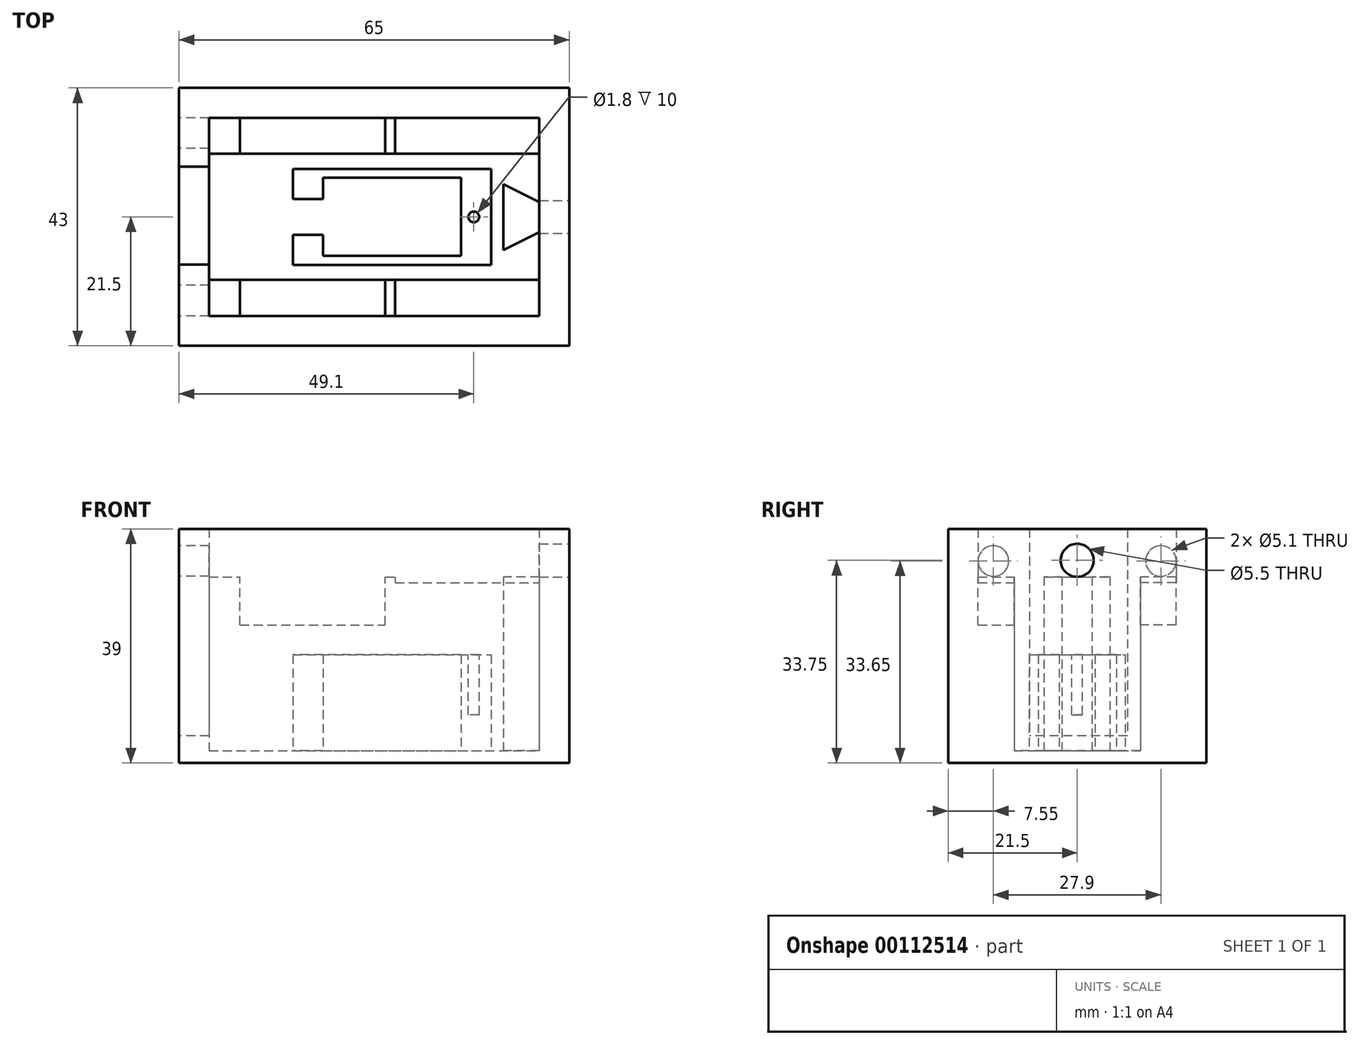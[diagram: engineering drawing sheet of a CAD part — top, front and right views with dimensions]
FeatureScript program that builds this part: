
annotation { "Feature Type Name" : "Feature", "Feature Type Description" : "" }
export const myFeature = defineFeature(function(context is Context, id is Id, definition is map)
    precondition{}
    {
        {
            var Q0;
            Q0=qCreatedBy(makeId("Top.planeOp"),FACE);
            var sketch = newSketch(context, id + "F0", { "sketchPlane" : qUnion([Q0])});
            skLineSegment(sketch, "E0.bottom", {"start": v(-32.5, 21.5) * mm, "end": v(32.5, 21.5) * mm});
            skLineSegment(sketch, "E0.top", {"start": v(-32.5, -21.5) * mm, "end": v(32.5, -21.5) * mm});
            skLineSegment(sketch, "E0.left", {"start": v(-32.5, 21.5) * mm, "end": v(-32.5, -21.5) * mm});
            skLineSegment(sketch, "E0.right", {"start": v(32.5, 21.5) * mm, "end": v(32.5, -21.5) * mm});
            skPoint(sketch, "E0.middle", {"position": v(0, 0) * mm});
            skSolve(sketch);
        }
        {
            var Q0;
            Q0 = qSketchRegion(id + "F0", true);
            extrude(context, id + "F1", {"entities" : qUnion([Q0]), "oppositeDirection" : true, "depth" : 2 * mm});
        }
        {
            var Q0;
            Q0=makeQuery(id+"F0.imprint","IMPRINT",FACE,{"disambiguationData":[TD([[makeQuery(id+"F0.imprint","IMPRINT",EDGE,{"derivedFrom":sQuery(id+"F0.wireOp",EDGE,"E0.bottom")}),-1.0]])]});
            var sketch = newSketch(context, id + "F2", { "sketchPlane" : qUnion([Q0])});
            skLineSegment(sketch, "E1", {"start": v(-32.5, 21.5) * mm, "end": v(-32.5, -21.5) * mm});
            skLineSegment(sketch, "E2", {"start": v(-32.5, -21.5) * mm, "end": v(32.5, -21.5) * mm});
            skLineSegment(sketch, "E3", {"start": v(32.5, -21.5) * mm, "end": v(32.5, 21.5) * mm});
            skLineSegment(sketch, "E4", {"start": v(32.5, 21.5) * mm, "end": v(-32.5, 21.5) * mm});
            skLineSegment(sketch, "E5", {"start": v(-27.5, 16.5) * mm, "end": v(-27.5, -16.5) * mm});
            skLineSegment(sketch, "E6", {"start": v(-27.5, -16.5) * mm, "end": v(27.5, -16.5) * mm});
            skLineSegment(sketch, "E7", {"start": v(27.5, -16.5) * mm, "end": v(27.5, 16.5) * mm});
            skLineSegment(sketch, "E8", {"start": v(27.5, 16.5) * mm, "end": v(-27.5, 16.5) * mm});
            skSolve(sketch);
        }
        {
            var Q0;
            Q0=makeQuery(id+"F2.imprint","IMPRINT",FACE,{"disambiguationData":[TD([[makeQuery(id+"F2.imprint","IMPRINT",EDGE,{"derivedFrom":sQuery(id+"F2.wireOp",EDGE,"E1")}),1.0]])]});
            extrude(context, id + "F3", {"entities" : qUnion([Q0]), "operationType" : NewBodyOperationType.ADD, "depth" : 37 * mm});
        }
        {
            var Q0;
            Q0=makeQuery(id+"F1.opExtrude","CAP_FACE",FACE,{"disambiguationData":[OSD([sQuery(id+"F0.wireOp",EDGE,"E0.bottom"),sQuery(id+"F0.wireOp",EDGE,"E0.top"),sQuery(id+"F0.wireOp",EDGE,"E0.left"),sQuery(id+"F0.wireOp",EDGE,"E0.right")])],"isStart":true});
            var sketch = newSketch(context, id + "F4", { "sketchPlane" : qUnion([Q0])});
            skLineSegment(sketch, "E9.bottom", {"start": v(-13.5, -8) * mm, "end": v(19.5, -8) * mm});
            skLineSegment(sketch, "E9.top", {"start": v(-13.5, 8) * mm, "end": v(19.5, 8) * mm});
            skLineSegment(sketch, "E9.left", {"start": v(-13.5, -8) * mm, "end": v(-13.5, 8) * mm});
            skLineSegment(sketch, "E9.right", {"start": v(19.5, -8) * mm, "end": v(19.5, 8) * mm});
            skPoint(sketch, "E9.middle", {"position": v(3, 0) * mm});
            skLineSegment(sketch, "E10", {"start": v(14.5, -6.5) * mm, "end": v(14.5, 6.5) * mm});
            skLineSegment(sketch, "E11", {"start": v(14.5, 6.5) * mm, "end": v(-8.5, 6.5) * mm});
            skLineSegment(sketch, "E12", {"start": v(-8.5, 6.5) * mm, "end": v(-8.5, -6.5) * mm});
            skLineSegment(sketch, "E13", {"start": v(-8.5, -6.5) * mm, "end": v(14.5, -6.5) * mm});
            skSolve(sketch);
        }
        {
            var Q0;
            Q0=makeQuery(id+"F4.imprint","IMPRINT",FACE,{"disambiguationData":[TD([[makeQuery(id+"F4.imprint","IMPRINT",EDGE,{"derivedFrom":sQuery(id+"F4.wireOp",EDGE,"E9.bottom")}),1.0]])]});
            extrude(context, id + "F5", {"entities" : qUnion([Q0]), "operationType" : NewBodyOperationType.ADD, "depth" : 16 * mm});
        }
        {
            var Q0;
            Q0=makeQuery(id+"F5.opExtrude","CAP_FACE",FACE,{"disambiguationData":[OSD([sQuery(id+"F4.wireOp",EDGE,"E9.bottom"),sQuery(id+"F4.wireOp",EDGE,"E9.top"),sQuery(id+"F4.wireOp",EDGE,"E9.left"),sQuery(id+"F4.wireOp",EDGE,"E9.right"),sQuery(id+"F4.wireOp",EDGE,"E10"),sQuery(id+"F4.wireOp",EDGE,"E11"),sQuery(id+"F4.wireOp",EDGE,"E12"),sQuery(id+"F4.wireOp",EDGE,"E13")])],"isStart":false});
            var sketch = newSketch(context, id + "F6", { "sketchPlane" : qUnion([Q0])});
            skCircle(sketch, "E14", {"center": v(16.6, 0) * mm, "radius": 0.9 * mm});
            skCircle(sketch, "E15", {"center": v(-10.6, 0) * mm, "radius": 0.9 * mm});
            skSolve(sketch);
        }
        {
            var Q0;
            Q0=makeQuery(id+"F6.imprint","IMPRINT",FACE,{"disambiguationData":[TD([[makeQuery(id+"F6.imprint","IMPRINT",EDGE,{"derivedFrom":sQuery(id+"F6.wireOp",EDGE,"E14")}),1.0]])]});
            var Q1;
            Q1=makeQuery(id+"F6.imprint","IMPRINT",FACE,{"disambiguationData":[TD([[makeQuery(id+"F6.imprint","IMPRINT",EDGE,{"derivedFrom":sQuery(id+"F6.wireOp",EDGE,"E15")}),1.0]])]});
            var Q2;
            Q2=sQuery(id+"F6.wireOp",EDGE,"E14");
            extrude(context, id + "F7", {"entities" : qUnion([Q0, Q1]), "operationType" : NewBodyOperationType.REMOVE, "surfaceEntities" : qUnion([Q2]), "oppositeDirection" : true, "depth" : 10 * mm});
        }
        {
            var Q0;
            Q0=makeQuery(id+"F5.boolean.opBoolean","SPLIT",FACE,{"disambiguationData":[TD([makeQuery(id+"F3.opExtrude","SWEPT_FACE",FACE,{"disambiguationData":[OSD([sQuery(id+"F2.wireOp",EDGE,"E5")])]})])],"derivedFrom":makeQuery(id+"F1.opExtrude","CAP_FACE",FACE,{"disambiguationData":[OSD([sQuery(id+"F0.wireOp",EDGE,"E0.bottom"),sQuery(id+"F0.wireOp",EDGE,"E0.top"),sQuery(id+"F0.wireOp",EDGE,"E0.left"),sQuery(id+"F0.wireOp",EDGE,"E0.right")])],"isStart":true})});
            var sketch = newSketch(context, id + "F8", { "sketchPlane" : qUnion([Q0])});
            skLineSegment(sketch, "E16.bottom", {"start": v(-27.5, -16.5) * mm, "end": v(27.5, -16.5) * mm});
            skLineSegment(sketch, "E16.top", {"start": v(-27.5, -10.5) * mm, "end": v(27.5, -10.5) * mm});
            skLineSegment(sketch, "E16.left", {"start": v(-27.5, -16.5) * mm, "end": v(-27.5, -10.5) * mm});
            skLineSegment(sketch, "E16.right", {"start": v(27.5, -16.5) * mm, "end": v(27.5, -10.5) * mm});
            skLineSegment(sketch, "E17.bottom", {"start": v(27.5, 16.5) * mm, "end": v(-27.5, 16.5) * mm});
            skLineSegment(sketch, "E17.top", {"start": v(27.5, 10.5) * mm, "end": v(-27.5, 10.5) * mm});
            skLineSegment(sketch, "E17.left", {"start": v(27.5, 16.5) * mm, "end": v(27.5, 10.5) * mm});
            skLineSegment(sketch, "E17.right", {"start": v(-27.5, 16.5) * mm, "end": v(-27.5, 10.5) * mm});
            skSolve(sketch);
        }
        {
            var Q0;
            Q0 = qSketchRegion(id + "F8", true);
            extrude(context, id + "F9", {"entities" : qUnion([Q0]), "operationType" : NewBodyOperationType.ADD, "depth" : 28 * mm});
        }
        {
            var Q0;
            Q0=makeQuery(id+"F3.boolean.opBoolean","MERGE",FACE,{"derivedFrom":[makeQuery(id+"F1.opExtrude","SWEPT_FACE",FACE,{"disambiguationData":[OSD([sQuery(id+"F0.wireOp",EDGE,"E0.left")])]}),makeQuery(id+"F3.opExtrude","SWEPT_FACE",FACE,{"disambiguationData":[OSD([sQuery(id+"F2.wireOp",EDGE,"E1")])]})]});
            var sketch = newSketch(context, id + "F10", { "sketchPlane" : qUnion([Q0])});
            skCircle(sketch, "E18", {"center": v(13.95, 31.65) * mm, "radius": 2.55 * mm});
            skCircle(sketch, "E19", {"center": v(-13.95, 31.65) * mm, "radius": 2.55 * mm});
            skSolve(sketch);
        }
        {
            var Q0;
            Q0=makeQuery(id+"F10.imprint","IMPRINT",FACE,{"disambiguationData":[TD([[makeQuery(id+"F10.imprint","IMPRINT",EDGE,{"derivedFrom":sQuery(id+"F10.wireOp",EDGE,"E18")}),1.0]])]});
            var Q1;
            Q1=makeQuery(id+"F10.imprint","IMPRINT",FACE,{"disambiguationData":[TD([[makeQuery(id+"F10.imprint","IMPRINT",EDGE,{"derivedFrom":sQuery(id+"F10.wireOp",EDGE,"E19")}),1.0]])]});
            extrude(context, id + "F11", {"entities" : qUnion([Q0, Q1]), "operationType" : NewBodyOperationType.REMOVE, "oppositeDirection" : true, "depth" : 25 * mm});
        }
        {
            var Q0;
            Q0=makeQuery(id+"F3.boolean.opBoolean","MERGE",FACE,{"derivedFrom":[makeQuery(id+"F1.opExtrude","SWEPT_FACE",FACE,{"disambiguationData":[OSD([sQuery(id+"F0.wireOp",EDGE,"E0.right")])]}),makeQuery(id+"F3.opExtrude","SWEPT_FACE",FACE,{"disambiguationData":[OSD([sQuery(id+"F2.wireOp",EDGE,"E3")])]})]});
            var sketch = newSketch(context, id + "F12", { "sketchPlane" : qUnion([Q0])});
            skCircle(sketch, "E20", {"center": v(0, 31.75) * mm, "radius": 2.75 * mm});
            skSolve(sketch);
        }
        {
            var Q0;
            Q0=makeQuery(id+"F12.imprint","IMPRINT",FACE,{"disambiguationData":[TD([[makeQuery(id+"F12.imprint","IMPRINT",EDGE,{"derivedFrom":sQuery(id+"F12.wireOp",EDGE,"E20")}),1.0]])]});
            extrude(context, id + "F13", {"entities" : qUnion([Q0]), "operationType" : NewBodyOperationType.REMOVE, "oppositeDirection" : true, "depth" : 25 * mm});
        }
        {
            var Q0;
            Q0=makeQuery(id+"F5.boolean.opBoolean","SPLIT",FACE,{"disambiguationData":[TD([makeQuery(id+"F3.opExtrude","SWEPT_FACE",FACE,{"disambiguationData":[OSD([sQuery(id+"F2.wireOp",EDGE,"E5")])]})])],"derivedFrom":makeQuery(id+"F1.opExtrude","CAP_FACE",FACE,{"disambiguationData":[OSD([sQuery(id+"F0.wireOp",EDGE,"E0.bottom"),sQuery(id+"F0.wireOp",EDGE,"E0.top"),sQuery(id+"F0.wireOp",EDGE,"E0.left"),sQuery(id+"F0.wireOp",EDGE,"E0.right")])],"isStart":true})});
            var sketch = newSketch(context, id + "F14", { "sketchPlane" : qUnion([Q0])});
            skLineSegment(sketch, "E21", {"start": v(27.5, -2.54) * mm, "end": v(21.5, -5.54) * mm});
            skLineSegment(sketch, "E22", {"start": v(21.5, -5.54) * mm, "end": v(21.5, 5.46) * mm});
            skLineSegment(sketch, "E23", {"start": v(21.5, 5.46) * mm, "end": v(27.5, 2.46) * mm});
            skLineSegment(sketch, "E24", {"start": v(27.5, -2.54) * mm, "end": v(27.5, 2.46) * mm});
            skSolve(sketch);
        }
        {
            var Q0;
            Q0=makeQuery(id+"F14.imprint","IMPRINT",FACE,{"disambiguationData":[TD([[makeQuery(id+"F14.imprint","IMPRINT",EDGE,{"derivedFrom":sQuery(id+"F14.wireOp",EDGE,"E21")}),-1.0]])]});
            extrude(context, id + "F15", {"entities" : qUnion([Q0]), "operationType" : NewBodyOperationType.ADD, "depth" : 29 * mm});
        }
        {
            var Q0;
            Q0=makeQuery(id+"F9.opExtrude","CAP_FACE",FACE,{"disambiguationData":[OSD([sQuery(id+"F8.wireOp",EDGE,"E16.bottom"),sQuery(id+"F8.wireOp",EDGE,"E16.top"),sQuery(id+"F8.wireOp",EDGE,"E16.left"),sQuery(id+"F8.wireOp",EDGE,"E16.right")])],"isStart":false});
            var sketch = newSketch(context, id + "F16", { "sketchPlane" : qUnion([Q0])});
            skLineSegment(sketch, "E25.bottom", {"start": v(-27.5, -16.5) * mm, "end": v(3.5, -16.5) * mm});
            skLineSegment(sketch, "E25.top", {"start": v(-27.5, -10.5) * mm, "end": v(3.5, -10.5) * mm});
            skLineSegment(sketch, "E25.left", {"start": v(-27.5, -16.5) * mm, "end": v(-27.5, -10.5) * mm});
            skLineSegment(sketch, "E25.right", {"start": v(3.5, -16.5) * mm, "end": v(3.5, -10.5) * mm});
            skLineSegment(sketch, "E26.bottom", {"start": v(-27.5, 16.5) * mm, "end": v(3.5, 16.5) * mm});
            skLineSegment(sketch, "E26.top", {"start": v(-27.5, 10.5) * mm, "end": v(3.5, 10.5) * mm});
            skLineSegment(sketch, "E26.left", {"start": v(-27.5, 16.5) * mm, "end": v(-27.5, 10.5) * mm});
            skLineSegment(sketch, "E26.right", {"start": v(3.5, 16.5) * mm, "end": v(3.5, 10.5) * mm});
            skSolve(sketch);
        }
        {
            var Q0;
            Q0=makeQuery(id+"F16.imprint","IMPRINT",FACE,{"disambiguationData":[TD([[makeQuery(id+"F16.imprint","IMPRINT",EDGE,{"derivedFrom":sQuery(id+"F16.wireOp",EDGE,"E25.bottom")}),1.0]])]});
            var Q1;
            Q1=makeQuery(id+"F16.imprint","IMPRINT",FACE,{"disambiguationData":[TD([[makeQuery(id+"F16.imprint","IMPRINT",EDGE,{"derivedFrom":sQuery(id+"F16.wireOp",EDGE,"E26.bottom")}),-1.0]])]});
            extrude(context, id + "F17", {"entities" : qUnion([Q0, Q1]), "operationType" : NewBodyOperationType.ADD, "depth" : 1 * mm});
        }
        {
            var Q0;
            Q0=makeQuery(id+"F3.boolean.opBoolean","MERGE",FACE,{"derivedFrom":[makeQuery(id+"F1.opExtrude","SWEPT_FACE",FACE,{"disambiguationData":[OSD([sQuery(id+"F0.wireOp",EDGE,"E0.left")])]}),makeQuery(id+"F3.opExtrude","SWEPT_FACE",FACE,{"disambiguationData":[OSD([sQuery(id+"F2.wireOp",EDGE,"E1")])]})]});
            var sketch = newSketch(context, id + "F18", { "sketchPlane" : qUnion([Q0])});
            skLineSegment(sketch, "E27.bottom", {"start": v(-8.39, 37) * mm, "end": v(7.96, 37) * mm});
            skLineSegment(sketch, "E27.top", {"start": v(-8.39, 2.5) * mm, "end": v(7.96, 2.5) * mm});
            skLineSegment(sketch, "E27.left", {"start": v(-8.39, 37) * mm, "end": v(-8.39, 2.5) * mm});
            skLineSegment(sketch, "E27.right", {"start": v(7.96, 37) * mm, "end": v(7.96, 2.5) * mm});
            skSolve(sketch);
        }
        {
            var Q0;
            Q0=makeQuery(id+"F18.imprint","IMPRINT",FACE,{"disambiguationData":[TD([[makeQuery(id+"F18.imprint","IMPRINT",EDGE,{"derivedFrom":sQuery(id+"F18.wireOp",EDGE,"E27.bottom")}),-1.0]])]});
            extrude(context, id + "F19", {"entities" : qUnion([Q0]), "operationType" : NewBodyOperationType.REMOVE, "oppositeDirection" : true, "depth" : 5 * mm});
        }
        {
            var Q0;
            Q0=makeQuery(id+"F17.opExtrude","CAP_FACE",FACE,{"disambiguationData":[OSD([sQuery(id+"F16.wireOp",EDGE,"E26.bottom"),sQuery(id+"F16.wireOp",EDGE,"E26.top"),sQuery(id+"F16.wireOp",EDGE,"E26.left"),sQuery(id+"F16.wireOp",EDGE,"E26.right")])],"isStart":false});
            var sketch = newSketch(context, id + "F20", { "sketchPlane" : qUnion([Q0])});
            skLineSegment(sketch, "E28.bottom", {"start": v(-22.35, 16.5) * mm, "end": v(1.87, 16.5) * mm});
            skLineSegment(sketch, "E28.top", {"start": v(-22.35, 10.5) * mm, "end": v(1.87, 10.5) * mm});
            skLineSegment(sketch, "E28.left", {"start": v(-22.35, 16.5) * mm, "end": v(-22.35, 10.5) * mm});
            skLineSegment(sketch, "E28.right", {"start": v(1.87, 16.5) * mm, "end": v(1.87, 10.5) * mm});
            skLineSegment(sketch, "E29.MirrorCS", {"start": v(1.87, -16.5) * mm, "end": v(1.87, -10.5) * mm});
            skLineSegment(sketch, "E30.MirrorCS", {"start": v(-22.35, -16.5) * mm, "end": v(-22.35, -10.5) * mm});
            skLineSegment(sketch, "E31.MirrorCS", {"start": v(-22.35, -16.5) * mm, "end": v(1.87, -16.5) * mm});
            skLineSegment(sketch, "E32.MirrorCS", {"start": v(-22.35, -10.5) * mm, "end": v(1.87, -10.5) * mm});
            skSolve(sketch);
        }
        {
            var Q0;
            Q0 = qSketchRegion(id + "F20", true);
            extrude(context, id + "F21", {"entities" : qUnion([Q0]), "operationType" : NewBodyOperationType.REMOVE, "oppositeDirection" : true, "depth" : 8 * mm});
        }
        {
            var Q0;
            Q0=makeQuery(id+"F5.opExtrude","SWEPT_FACE",FACE,{"disambiguationData":[OSD([sQuery(id+"F4.wireOp",EDGE,"E9.left")])]});
            var sketch = newSketch(context, id + "F22", { "sketchPlane" : qUnion([Q0])});
            skLineSegment(sketch, "E33.bottom", {"start": v(-3, 16) * mm, "end": v(3, 16) * mm});
            skLineSegment(sketch, "E33.top", {"start": v(-3, 0) * mm, "end": v(3, 0) * mm});
            skLineSegment(sketch, "E33.left", {"start": v(-3, 16) * mm, "end": v(-3, 0) * mm});
            skLineSegment(sketch, "E33.right", {"start": v(3, 16) * mm, "end": v(3, 0) * mm});
            skSolve(sketch);
        }
        {
            var Q0;
            Q0 = qSketchRegion(id + "F22", true);
            extrude(context, id + "F23", {"entities" : qUnion([Q0]), "operationType" : NewBodyOperationType.REMOVE, "oppositeDirection" : true, "depth" : 5 * mm});
        }
    });
